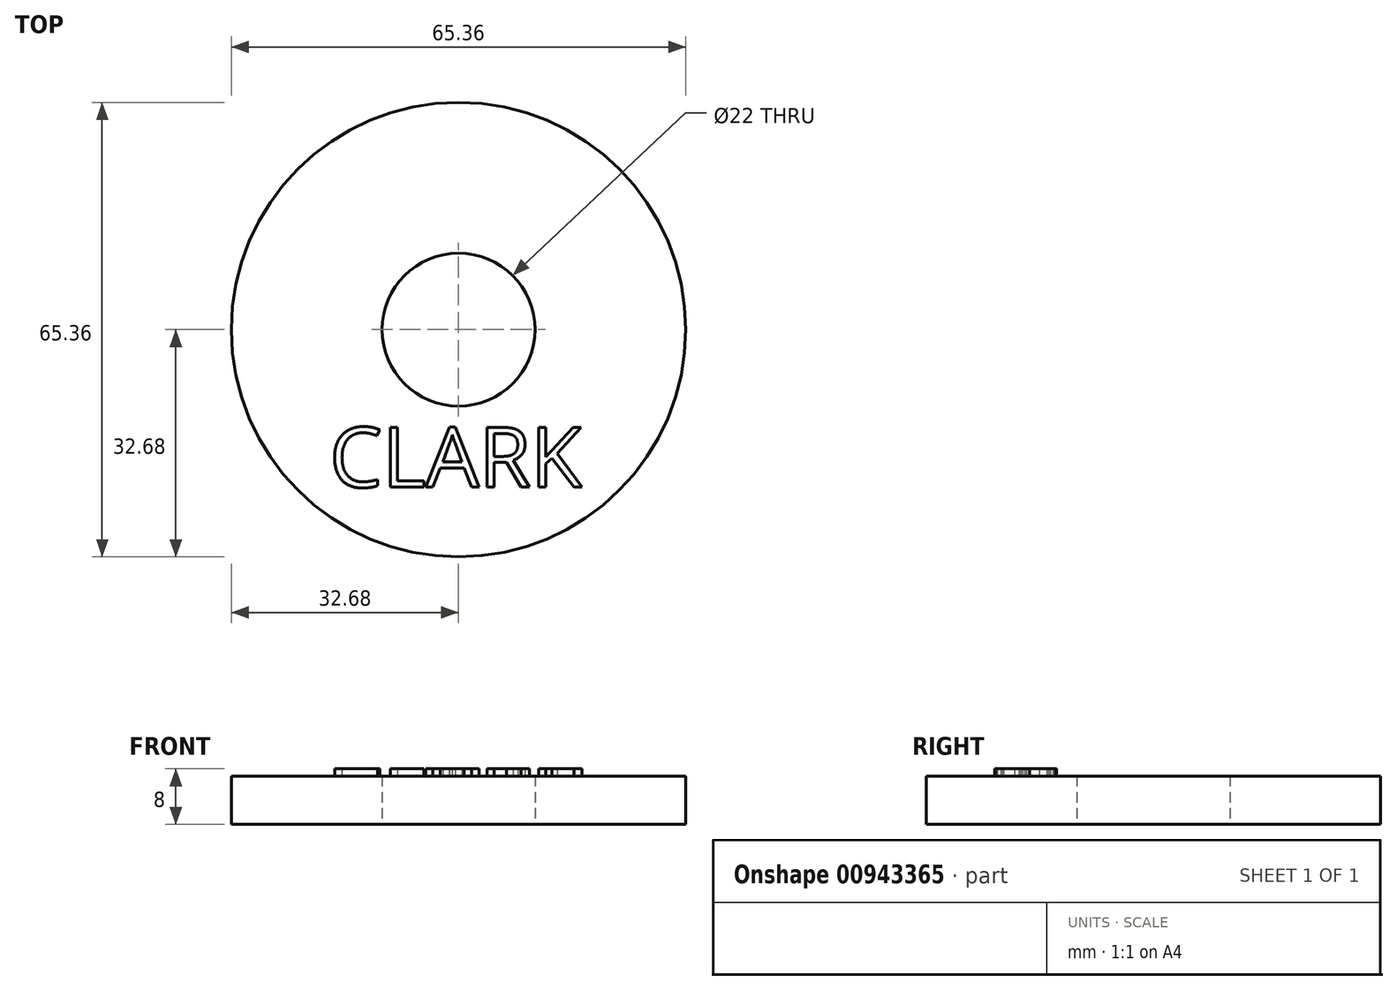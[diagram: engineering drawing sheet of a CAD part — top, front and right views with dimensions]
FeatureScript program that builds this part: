
annotation { "Feature Type Name" : "Feature", "Feature Type Description" : "" }
export const myFeature = defineFeature(function(context is Context, id is Id, definition is map)
    precondition{}
    {
        {
            var Q0;
            Q0=qCreatedBy(makeId("Top.planeOp"),FACE);
            var sketch = newSketch(context, id + "F0", { "sketchPlane" : qUnion([Q0])});
            skCircle(sketch, "E0", {"center": v(0, 0) * mm, "radius": 11 * mm});
            skCircle(sketch, "E1", {"center": v(0, 0) * mm, "radius": 32.68 * mm});
            skSolve(sketch);
        }
        {
            var Q0;
            Q0=makeQuery(id+"F0.imprint","IMPRINT",FACE,{"disambiguationData":[TD([[makeQuery(id+"F0.imprint","IMPRINT",EDGE,{"derivedFrom":sQuery(id+"F0.wireOp",EDGE,"E0")}),-1.0]])]});
            extrude(context, id + "F1", {"entities" : qUnion([Q0]), "depth" : 6.96 * mm, "offsetDistance" : 25 * mm});
        }
        {
            var Q0;
            Q0=qCreatedBy(makeId("Top.planeOp"),FACE);
            var sketch = newSketch(context, id + "F2", { "sketchPlane" : qUnion([Q0])});
            skText(sketch, "E2", { "text": "CLARK", "fontName": "OpenSans-Regular.ttf"});
            const initialGuessF2  = {"E2": [-0.01857, -0.02267, 1, 0, 0.00868]};
            skSetInitialGuess(sketch, initialGuessF2);
            skSolve(sketch);
        }
        {
            var Q0;
            Q0 = qSketchRegion(id + "F2", true);
            extrude(context, id + "F3", {"entities" : qUnion([Q0]), "operationType" : NewBodyOperationType.ADD, "depth" : 8 * mm, "offsetDistance" : 25 * mm});
        }
    });
